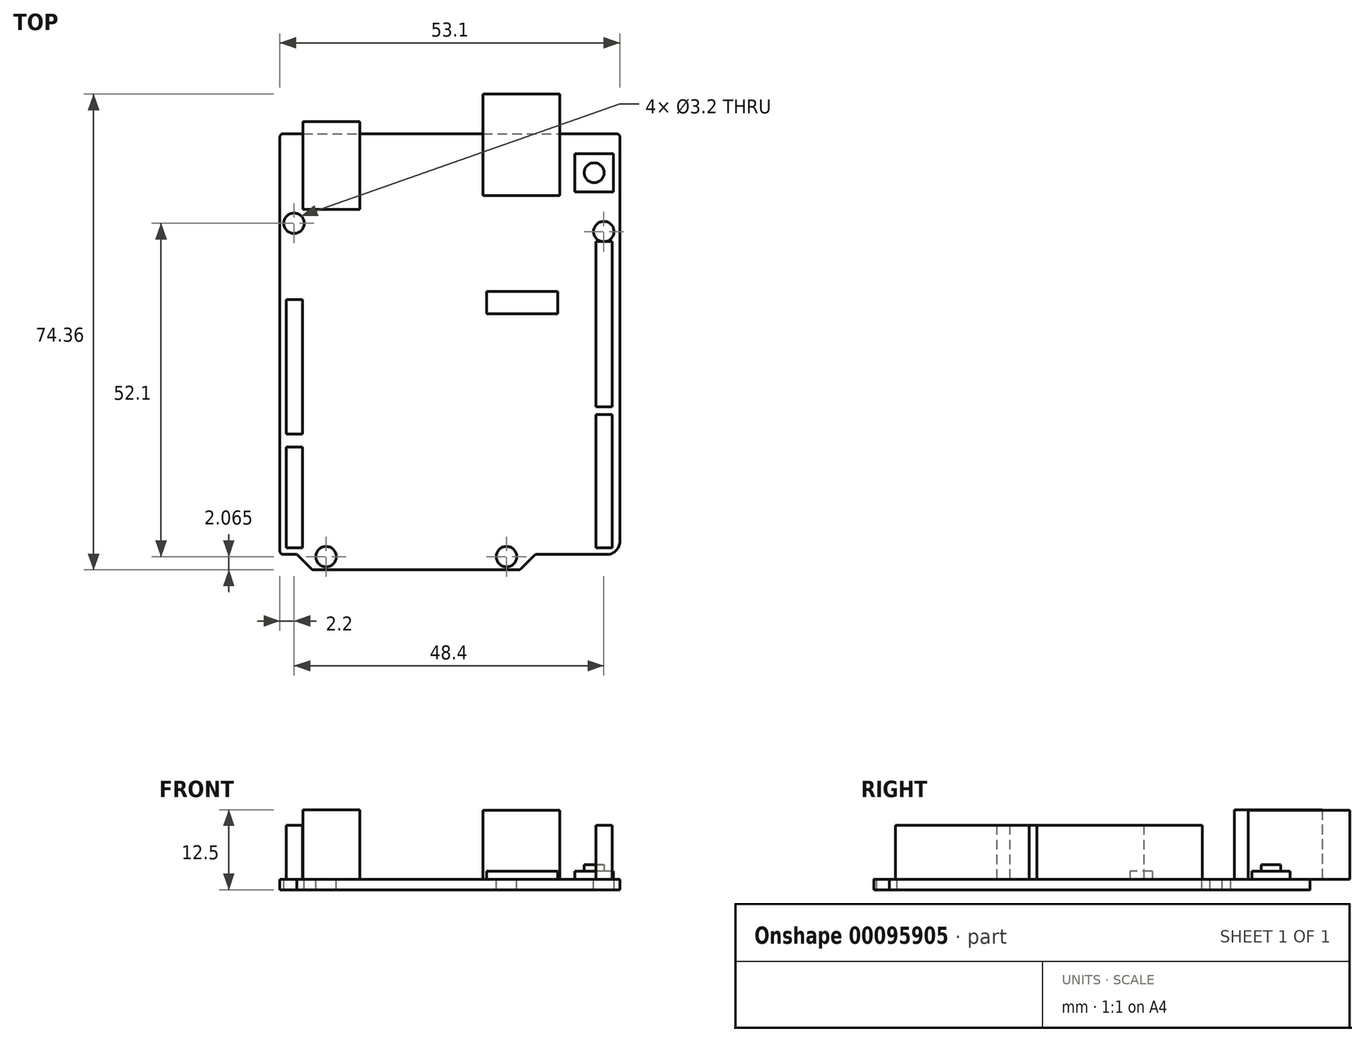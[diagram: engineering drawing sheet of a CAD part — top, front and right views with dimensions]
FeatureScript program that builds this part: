
annotation { "Feature Type Name" : "Feature", "Feature Type Description" : "" }
export const myFeature = defineFeature(function(context is Context, id is Id, definition is map)
    precondition{}
    {
        {
            var Q0;
            Q0=qCreatedBy(makeId("Top.planeOp"),FACE);
            var sketch = newSketch(context, id + "F0", { "sketchPlane" : qUnion([Q0])});
            skLineSegment(sketch, "E0", {"start": v(-26.05, 32.87) * mm, "end": v(26.05, 32.88) * mm});
            skLineSegment(sketch, "E1", {"start": v(26.55, 32.38) * mm, "end": v(26.55, -30.87) * mm});
            skLineSegment(sketch, "E2", {"start": v(24.55, -32.87) * mm, "end": v(13.56, -32.87) * mm});
            skLineSegment(sketch, "E3", {"start": v(13.2, -33.02) * mm, "end": v(11.09, -35.14) * mm});
            skLineSegment(sketch, "E4", {"start": v(10.73, -35.28) * mm, "end": v(-21.28, -35.29) * mm});
            skLineSegment(sketch, "E5", {"start": v(-21.64, -35.14) * mm, "end": v(-23.9, -32.88) * mm});
            skLineSegment(sketch, "E6", {"start": v(-23.9, -32.88) * mm, "end": v(-26.05, -32.88) * mm});
            skLineSegment(sketch, "E7", {"start": v(-26.55, -32.38) * mm, "end": v(-26.55, 32.37) * mm});
            skPoint(sketch, "E8.visualSharp", {"position": v(-26.55, 32.87) * mm});
            skArc(sketch, "E8.filletArc", {"start": v(-26.05, 32.87) * mm, "mid": v(-26.4, 32.73) * mm, "end": v(-26.55, 32.37) * mm});
            skPoint(sketch, "E9.visualSharp", {"position": v(26.55, 32.88) * mm});
            skArc(sketch, "E9.filletArc", {"start": v(26.55, 32.38) * mm, "mid": v(26.4, 32.73) * mm, "end": v(26.05, 32.88) * mm});
            skPoint(sketch, "E10.visualSharp", {"position": v(-26.55, -32.88) * mm});
            skArc(sketch, "E10.filletArc", {"start": v(-26.55, -32.38) * mm, "mid": v(-26.4, -32.73) * mm, "end": v(-26.05, -32.88) * mm});
            skPoint(sketch, "E11.visualSharp", {"position": v(-21.49, -35.29) * mm});
            skArc(sketch, "E11.filletArc", {"start": v(-21.64, -35.14) * mm, "mid": v(-21.47, -35.25) * mm, "end": v(-21.28, -35.28) * mm});
            skPoint(sketch, "E12.visualSharp", {"position": v(10.94, -35.28) * mm});
            skArc(sketch, "E12.filletArc", {"start": v(10.73, -35.28) * mm, "mid": v(10.92, -35.25) * mm, "end": v(11.09, -35.14) * mm});
            skPoint(sketch, "E13.visualSharp", {"position": v(13.35, -32.87) * mm});
            skArc(sketch, "E13.filletArc", {"start": v(13.56, -32.87) * mm, "mid": v(13.37, -32.91) * mm, "end": v(13.2, -33.02) * mm});
            skPoint(sketch, "E14.visualSharp", {"position": v(26.55, -32.87) * mm});
            skArc(sketch, "E14.filletArc", {"start": v(24.55, -32.87) * mm, "mid": v(25.96, -32.29) * mm, "end": v(26.55, -30.87) * mm});
            skSolve(sketch);
        }
        {
            var Q0;
            Q0=qSketchRegion(id+"F0",true);
            extrude(context, id + "F1", {"entities" : qUnion([Q0]), "depth" : 1.6 * mm});
        }
        {
            var Q0;
            Q0=makeQuery(id+"F1.opExtrude","CAP_FACE",FACE,{"disambiguationData":[OSD([sQuery(id+"F0.wireOp",EDGE,"E0"),sQuery(id+"F0.wireOp",EDGE,"E1"),sQuery(id+"F0.wireOp",EDGE,"E2"),sQuery(id+"F0.wireOp",EDGE,"E3"),sQuery(id+"F0.wireOp",EDGE,"E4"),sQuery(id+"F0.wireOp",EDGE,"E5"),sQuery(id+"F0.wireOp",EDGE,"E6"),sQuery(id+"F0.wireOp",EDGE,"E7"),sQuery(id+"F0.wireOp",EDGE,"E8.filletArc"),sQuery(id+"F0.wireOp",EDGE,"E9.filletArc"),sQuery(id+"F0.wireOp",EDGE,"E10.filletArc"),sQuery(id+"F0.wireOp",EDGE,"E11.filletArc"),sQuery(id+"F0.wireOp",EDGE,"E12.filletArc"),sQuery(id+"F0.wireOp",EDGE,"E13.filletArc"),sQuery(id+"F0.wireOp",EDGE,"E14.filletArc")])],"isStart":false});
            var sketch = newSketch(context, id + "F2", { "sketchPlane" : qUnion([Q0])});
            skLineSegment(sketch, "E15.bottom", {"start": v(17.15, 39.08) * mm, "end": v(5.15, 39.08) * mm});
            skLineSegment(sketch, "E15.top", {"start": v(17.15, 23.2) * mm, "end": v(5.15, 23.2) * mm});
            skLineSegment(sketch, "E15.left", {"start": v(17.15, 39.08) * mm, "end": v(17.15, 23.2) * mm});
            skLineSegment(sketch, "E15.right", {"start": v(5.15, 39.08) * mm, "end": v(5.15, 23.2) * mm});
            skSolve(sketch);
        }
        {
            var Q0;
            Q0=qSketchRegion(id+"F2",true);
            extrude(context, id + "F3", {"entities" : qUnion([Q0]), "depth" : 10.82 * mm});
        }
        {
            var Q0;
            Q0=makeQuery(id+"F1.opExtrude","CAP_FACE",FACE,{"disambiguationData":[OSD([sQuery(id+"F0.wireOp",EDGE,"E0"),sQuery(id+"F0.wireOp",EDGE,"E1"),sQuery(id+"F0.wireOp",EDGE,"E2"),sQuery(id+"F0.wireOp",EDGE,"E3"),sQuery(id+"F0.wireOp",EDGE,"E4"),sQuery(id+"F0.wireOp",EDGE,"E5"),sQuery(id+"F0.wireOp",EDGE,"E6"),sQuery(id+"F0.wireOp",EDGE,"E7"),sQuery(id+"F0.wireOp",EDGE,"E8.filletArc"),sQuery(id+"F0.wireOp",EDGE,"E9.filletArc"),sQuery(id+"F0.wireOp",EDGE,"E10.filletArc"),sQuery(id+"F0.wireOp",EDGE,"E11.filletArc"),sQuery(id+"F0.wireOp",EDGE,"E12.filletArc"),sQuery(id+"F0.wireOp",EDGE,"E13.filletArc"),sQuery(id+"F0.wireOp",EDGE,"E14.filletArc")])],"isStart":false});
            var sketch = newSketch(context, id + "F4", { "sketchPlane" : qUnion([Q0])});
            skLineSegment(sketch, "E16.bottom", {"start": v(-14.05, 34.77) * mm, "end": v(-22.95, 34.77) * mm});
            skLineSegment(sketch, "E16.top", {"start": v(-14.05, 21.07) * mm, "end": v(-22.95, 21.07) * mm});
            skLineSegment(sketch, "E16.left", {"start": v(-14.05, 34.77) * mm, "end": v(-14.05, 21.07) * mm});
            skLineSegment(sketch, "E16.right", {"start": v(-22.95, 34.77) * mm, "end": v(-22.95, 21.07) * mm});
            skSolve(sketch);
        }
        {
            var Q0;
            Q0=qSketchRegion(id+"F4",true);
            extrude(context, id + "F5", {"entities" : qUnion([Q0]), "depth" : 10.9 * mm});
        }
        {
            var Q0;
            Q0=makeQuery(id+"F1.opExtrude","CAP_FACE",FACE,{"disambiguationData":[OSD([sQuery(id+"F0.wireOp",EDGE,"E0"),sQuery(id+"F0.wireOp",EDGE,"E1"),sQuery(id+"F0.wireOp",EDGE,"E2"),sQuery(id+"F0.wireOp",EDGE,"E3"),sQuery(id+"F0.wireOp",EDGE,"E4"),sQuery(id+"F0.wireOp",EDGE,"E5"),sQuery(id+"F0.wireOp",EDGE,"E6"),sQuery(id+"F0.wireOp",EDGE,"E7"),sQuery(id+"F0.wireOp",EDGE,"E8.filletArc"),sQuery(id+"F0.wireOp",EDGE,"E9.filletArc"),sQuery(id+"F0.wireOp",EDGE,"E10.filletArc"),sQuery(id+"F0.wireOp",EDGE,"E11.filletArc"),sQuery(id+"F0.wireOp",EDGE,"E12.filletArc"),sQuery(id+"F0.wireOp",EDGE,"E13.filletArc"),sQuery(id+"F0.wireOp",EDGE,"E14.filletArc")])],"isStart":false});
            var sketch = newSketch(context, id + "F6", { "sketchPlane" : qUnion([Q0])});
            skCircle(sketch, "E17", {"center": v(-19.35, -33.23) * mm, "radius": 1.6 * mm});
            skCircle(sketch, "E18", {"center": v(8.85, -33.22) * mm, "radius": 1.6 * mm});
            skCircle(sketch, "E19", {"center": v(24.05, 17.57) * mm, "radius": 1.6 * mm});
            skCircle(sketch, "E20", {"center": v(-24.35, 18.87) * mm, "radius": 1.6 * mm});
            skSolve(sketch);
        }
        {
            var Q0;
            Q0=qSketchRegion(id+"F6",true);
            extrude(context, id + "F7", {"entities" : qUnion([Q0]), "operationType" : NewBodyOperationType.REMOVE, "oppositeDirection" : true, "depth" : 3 * mm});
        }
        {
            var Q0;
            Q0=makeQuery(id+"F1.opExtrude","CAP_FACE",FACE,{"disambiguationData":[OSD([sQuery(id+"F0.wireOp",EDGE,"E0"),sQuery(id+"F0.wireOp",EDGE,"E1"),sQuery(id+"F0.wireOp",EDGE,"E2"),sQuery(id+"F0.wireOp",EDGE,"E3"),sQuery(id+"F0.wireOp",EDGE,"E4"),sQuery(id+"F0.wireOp",EDGE,"E5"),sQuery(id+"F0.wireOp",EDGE,"E6"),sQuery(id+"F0.wireOp",EDGE,"E7"),sQuery(id+"F0.wireOp",EDGE,"E8.filletArc"),sQuery(id+"F0.wireOp",EDGE,"E9.filletArc"),sQuery(id+"F0.wireOp",EDGE,"E10.filletArc"),sQuery(id+"F0.wireOp",EDGE,"E11.filletArc"),sQuery(id+"F0.wireOp",EDGE,"E12.filletArc"),sQuery(id+"F0.wireOp",EDGE,"E13.filletArc"),sQuery(id+"F0.wireOp",EDGE,"E14.filletArc")])],"isStart":false});
            var sketch = newSketch(context, id + "F8", { "sketchPlane" : qUnion([Q0])});
            skLineSegment(sketch, "E21.bottom", {"start": v(25.35, 16.03) * mm, "end": v(22.85, 16.03) * mm});
            skLineSegment(sketch, "E21.top", {"start": v(25.35, -9.82) * mm, "end": v(22.85, -9.82) * mm});
            skLineSegment(sketch, "E21.left", {"start": v(25.35, 16.03) * mm, "end": v(25.35, -9.82) * mm});
            skLineSegment(sketch, "E21.right", {"start": v(22.85, 16.03) * mm, "end": v(22.85, -9.82) * mm});
            skLineSegment(sketch, "E22.bottom", {"start": v(25.35, -11.02) * mm, "end": v(22.85, -11.02) * mm});
            skLineSegment(sketch, "E22.top", {"start": v(25.35, -31.87) * mm, "end": v(22.85, -31.87) * mm});
            skLineSegment(sketch, "E22.left", {"start": v(25.35, -11.02) * mm, "end": v(25.35, -31.87) * mm});
            skLineSegment(sketch, "E22.right", {"start": v(22.85, -11.02) * mm, "end": v(22.85, -31.87) * mm});
            skLineSegment(sketch, "E23.bottom", {"start": v(-23.05, 6.92) * mm, "end": v(-25.55, 6.92) * mm});
            skLineSegment(sketch, "E23.top", {"start": v(-23.05, -14.08) * mm, "end": v(-25.55, -14.08) * mm});
            skLineSegment(sketch, "E23.left", {"start": v(-23.05, 6.92) * mm, "end": v(-23.05, -14.08) * mm});
            skLineSegment(sketch, "E23.right", {"start": v(-25.55, 6.92) * mm, "end": v(-25.55, -14.08) * mm});
            skLineSegment(sketch, "E24.bottom", {"start": v(-23.05, -16.08) * mm, "end": v(-25.55, -16.08) * mm});
            skLineSegment(sketch, "E24.top", {"start": v(-23.05, -31.88) * mm, "end": v(-25.55, -31.88) * mm});
            skLineSegment(sketch, "E24.left", {"start": v(-23.05, -16.08) * mm, "end": v(-23.05, -31.88) * mm});
            skLineSegment(sketch, "E24.right", {"start": v(-25.55, -16.08) * mm, "end": v(-25.55, -31.88) * mm});
            skSolve(sketch);
        }
        {
            var Q0;
            Q0=qSketchRegion(id+"F8",true);
            extrude(context, id + "F9", {"entities" : qUnion([Q0]), "depth" : 8.5 * mm});
        }
        {
            var Q0;
            Q0=makeQuery(id+"F1.opExtrude","CAP_FACE",FACE,{"disambiguationData":[OSD([sQuery(id+"F0.wireOp",EDGE,"E0"),sQuery(id+"F0.wireOp",EDGE,"E1"),sQuery(id+"F0.wireOp",EDGE,"E2"),sQuery(id+"F0.wireOp",EDGE,"E3"),sQuery(id+"F0.wireOp",EDGE,"E4"),sQuery(id+"F0.wireOp",EDGE,"E5"),sQuery(id+"F0.wireOp",EDGE,"E6"),sQuery(id+"F0.wireOp",EDGE,"E7"),sQuery(id+"F0.wireOp",EDGE,"E8.filletArc"),sQuery(id+"F0.wireOp",EDGE,"E9.filletArc"),sQuery(id+"F0.wireOp",EDGE,"E10.filletArc"),sQuery(id+"F0.wireOp",EDGE,"E11.filletArc"),sQuery(id+"F0.wireOp",EDGE,"E12.filletArc"),sQuery(id+"F0.wireOp",EDGE,"E13.filletArc"),sQuery(id+"F0.wireOp",EDGE,"E14.filletArc")])],"isStart":false});
            var sketch = newSketch(context, id + "F10", { "sketchPlane" : qUnion([Q0])});
            skLineSegment(sketch, "E25.bottom", {"start": v(25.55, 29.78) * mm, "end": v(19.55, 29.78) * mm});
            skLineSegment(sketch, "E25.top", {"start": v(25.55, 23.78) * mm, "end": v(19.55, 23.78) * mm});
            skLineSegment(sketch, "E25.left", {"start": v(25.55, 29.78) * mm, "end": v(25.55, 23.78) * mm});
            skLineSegment(sketch, "E25.right", {"start": v(19.55, 29.78) * mm, "end": v(19.55, 23.78) * mm});
            skSolve(sketch);
        }
        {
            var Q0;
            Q0=qSketchRegion(id+"F10",true);
            extrude(context, id + "F11", {"entities" : qUnion([Q0]), "depth" : 1.3 * mm});
        }
        {
            var Q0;
            Q0=makeQuery(id+"F11.opExtrude","CAP_FACE",FACE,{"disambiguationData":[OSD([sQuery(id+"F10.wireOp",EDGE,"E25.bottom"),sQuery(id+"F10.wireOp",EDGE,"E25.top"),sQuery(id+"F10.wireOp",EDGE,"E25.left"),sQuery(id+"F10.wireOp",EDGE,"E25.right")])],"isStart":false});
            var sketch = newSketch(context, id + "F12", { "sketchPlane" : qUnion([Q0])});
            skCircle(sketch, "E26", {"center": v(22.55, 26.78) * mm, "radius": 1.55 * mm});
            skPoint(sketch, "E26.centerSnap0", {"position": v(22.55, 23.78) * mm});
            skSolve(sketch);
        }
        {
            var Q0;
            Q0=qSketchRegion(id+"F12",true);
            extrude(context, id + "F13", {"entities" : qUnion([Q0]), "operationType" : NewBodyOperationType.ADD, "depth" : 1 * mm});
        }
        {
            var Q0;
            Q0=makeQuery(id+"F1.opExtrude","CAP_FACE",FACE,{"disambiguationData":[OSD([sQuery(id+"F0.wireOp",EDGE,"E0"),sQuery(id+"F0.wireOp",EDGE,"E1"),sQuery(id+"F0.wireOp",EDGE,"E2"),sQuery(id+"F0.wireOp",EDGE,"E3"),sQuery(id+"F0.wireOp",EDGE,"E4"),sQuery(id+"F0.wireOp",EDGE,"E5"),sQuery(id+"F0.wireOp",EDGE,"E6"),sQuery(id+"F0.wireOp",EDGE,"E7"),sQuery(id+"F0.wireOp",EDGE,"E8.filletArc"),sQuery(id+"F0.wireOp",EDGE,"E9.filletArc"),sQuery(id+"F0.wireOp",EDGE,"E10.filletArc"),sQuery(id+"F0.wireOp",EDGE,"E11.filletArc"),sQuery(id+"F0.wireOp",EDGE,"E12.filletArc"),sQuery(id+"F0.wireOp",EDGE,"E13.filletArc"),sQuery(id+"F0.wireOp",EDGE,"E14.filletArc")])],"isStart":false});
            var sketch = newSketch(context, id + "F14", { "sketchPlane" : qUnion([Q0])});
            skLineSegment(sketch, "E27.bottom", {"start": v(5.75, 8.22) * mm, "end": v(16.85, 8.22) * mm});
            skLineSegment(sketch, "E27.top", {"start": v(5.75, 4.72) * mm, "end": v(16.85, 4.72) * mm});
            skLineSegment(sketch, "E27.left", {"start": v(5.75, 8.22) * mm, "end": v(5.75, 4.72) * mm});
            skLineSegment(sketch, "E27.right", {"start": v(16.85, 8.22) * mm, "end": v(16.85, 4.72) * mm});
            skSolve(sketch);
        }
        {
            var Q0;
            Q0=qSketchRegion(id+"F14",true);
            extrude(context, id + "F15", {"entities" : qUnion([Q0]), "depth" : 1.3 * mm});
        }
    });
